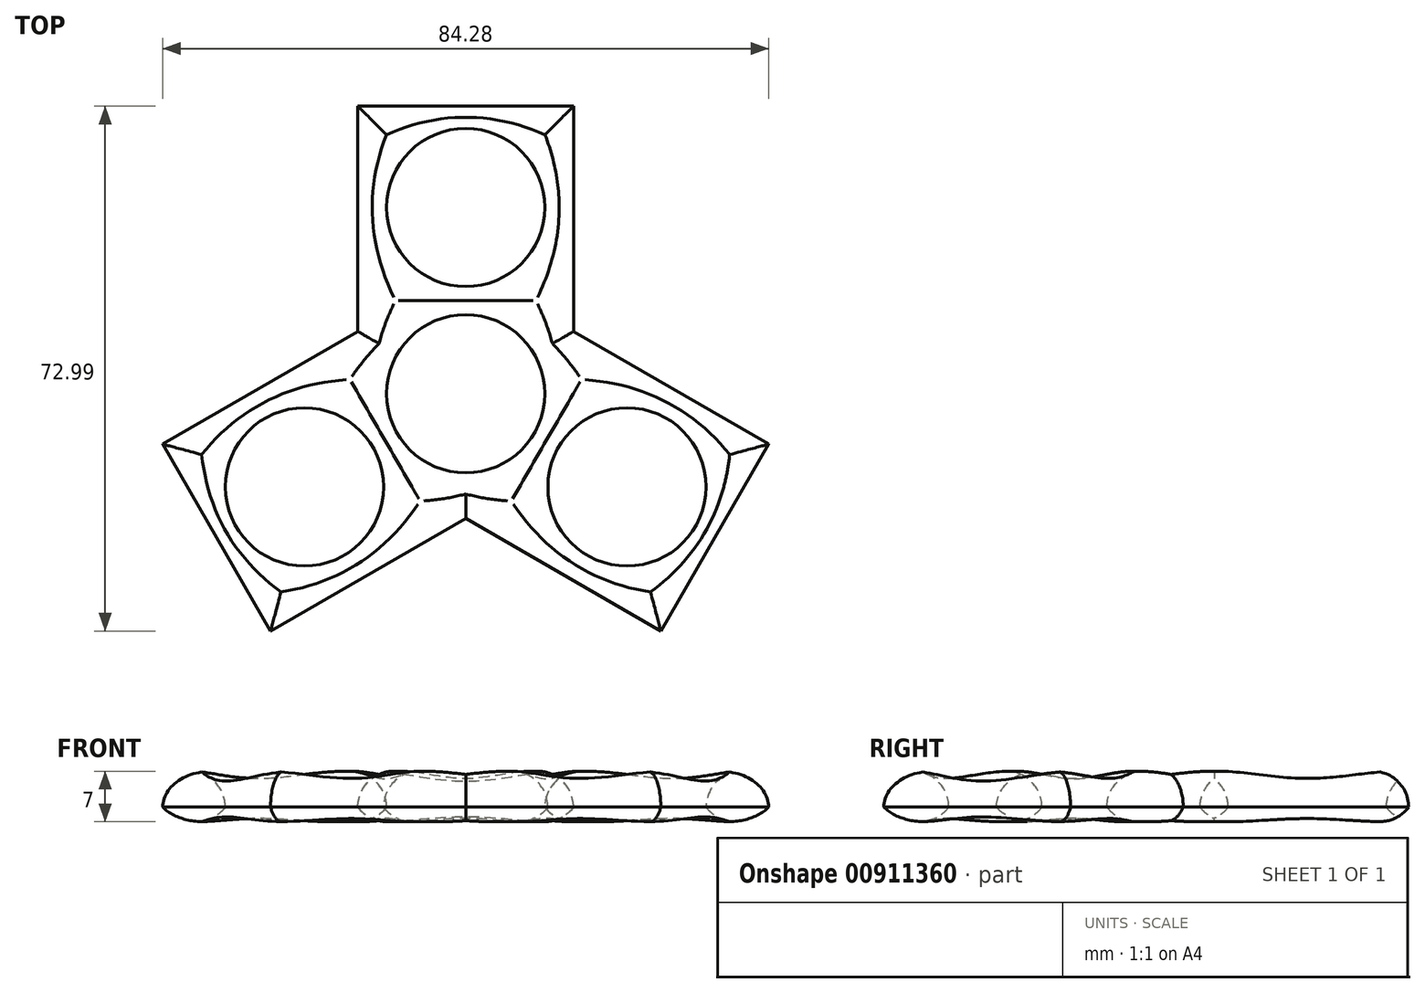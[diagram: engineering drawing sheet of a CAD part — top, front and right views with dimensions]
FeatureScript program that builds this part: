
annotation { "Feature Type Name" : "Feature", "Feature Type Description" : "" }
export const myFeature = defineFeature(function(context is Context, id is Id, definition is map)
    precondition{}
    {
        {
            var Q0;
            Q0=qCreatedBy(makeId("Top.planeOp"),FACE);
            var sketch = newSketch(context, id + "F0", { "sketchPlane" : qUnion([Q0])});
            skCircle(sketch, "E0", {"center": v(0, 0) * mm, "radius": 11 * mm});
            skLineSegment(sketch, "E1.bottom", {"start": v(0, 0) * mm, "end": v(15, 0) * mm});
            skLineSegment(sketch, "E1.top", {"start": v(0, 40) * mm, "end": v(15, 40) * mm});
            skLineSegment(sketch, "E1.left", {"start": v(0, 0) * mm, "end": v(0, 40) * mm});
            skLineSegment(sketch, "E1.right", {"start": v(15, 0) * mm, "end": v(15, 40) * mm});
            skLineSegment(sketch, "E2.bottom", {"start": v(0, 0) * mm, "end": v(-15, 0) * mm});
            skLineSegment(sketch, "E2.top", {"start": v(0, 40) * mm, "end": v(-15, 40) * mm});
            skLineSegment(sketch, "E2.right", {"start": v(-15, 0) * mm, "end": v(-15, 40) * mm});
            skLineSegment(sketch, "E3", {"start": v(0, 40) * mm, "end": v(0, 25.9) * mm});
            skCircle(sketch, "E4", {"center": v(0, 25.9) * mm, "radius": 11 * mm});
            skSolve(sketch);
        }
        {
            var Q0;
            {var subQ0=sQuery(id+"F0.wireOp",EDGE,"E2.top");Q0=makeQuery(id+"F0.imprint","IMPRINT",FACE,{"disambiguationData":[TD([[makeQuery(id+"F0.imprint","IMPRINT",EDGE,{"derivedFrom":subQ0}),1.0]])]});}
            var Q1;
            {var subQ9=sQuery(id+"F0.wireOp",EDGE,"E1.top");Q1=makeQuery(id+"F0.imprint","IMPRINT",FACE,{"disambiguationData":[TD([[makeQuery(id+"F0.imprint","IMPRINT",EDGE,{"derivedFrom":subQ9}),-1.0]])]});}
            extrude(context, id + "F1", {"entities" : qUnion([Q0, Q1]), "depth" : 7 * mm, "offsetDistance" : 25 * mm});
        }
        {
            var Q0;
            Q0=qCreatedBy(makeId("Front.planeOp"),FACE);
            var sketch = newSketch(context, id + "F2", { "sketchPlane" : qUnion([Q0])});
            skLineSegment(sketch, "E5", {"start": v(0, 30.21) * mm, "end": v(0, -19.5) * mm});
            skSolve(sketch);
        }
        {
            var Q0;
            Q0=makeQuery(id+"F1.opExtrude","SWEPT_BODY",BODY,{"disambiguationData":[OSD([sQuery(id+"F0.wireOp",EDGE,"E0"),sQuery(id+"F0.wireOp",EDGE,"E1.bottom"),sQuery(id+"F0.wireOp",EDGE,"E1.top"),sQuery(id+"F0.wireOp",EDGE,"E1.right"),sQuery(id+"F0.wireOp",EDGE,"E2.bottom"),sQuery(id+"F0.wireOp",EDGE,"E2.top"),sQuery(id+"F0.wireOp",EDGE,"E2.right"),sQuery(id+"F0.wireOp",EDGE,"E4")])]});
            var Q1;
            Q1=sQuery(id+"F2.wireOp",EDGE,"E5");
            var Q2;
            Q2=sQuery(id+"F2.wireOp",EDGE,"E5");
            transform(context, id + "F3", {"entities" : qUnion([Q0]), "transformType" : TransformType.ROTATION, "transformAxis" : qUnion([Q2]), "angle" : 120 * degree, "makeCopy" : true});
        }
        {
            var Q0;
            Q0=makeQuery(id+"F1.opExtrude","SWEPT_BODY",BODY,{"disambiguationData":[OSD([sQuery(id+"F0.wireOp",EDGE,"E0"),sQuery(id+"F0.wireOp",EDGE,"E1.bottom"),sQuery(id+"F0.wireOp",EDGE,"E1.top"),sQuery(id+"F0.wireOp",EDGE,"E1.right"),sQuery(id+"F0.wireOp",EDGE,"E2.bottom"),sQuery(id+"F0.wireOp",EDGE,"E2.top"),sQuery(id+"F0.wireOp",EDGE,"E2.right"),sQuery(id+"F0.wireOp",EDGE,"E4")])]});
            var Q1;
            Q1=sQuery(id+"F2.wireOp",EDGE,"E5");
            transform(context, id + "F4", {"entities" : qUnion([Q0]), "transformType" : TransformType.ROTATION, "transformAxis" : qUnion([Q1]), "angle" : 240 * degree, "makeCopy" : true});
        }
        {
            var Q0;
            Q0=makeQuery(id+"F1.opExtrude","SWEPT_BODY",BODY,{"disambiguationData":[OSD([sQuery(id+"F0.wireOp",EDGE,"E0"),sQuery(id+"F0.wireOp",EDGE,"E1.bottom"),sQuery(id+"F0.wireOp",EDGE,"E1.top"),sQuery(id+"F0.wireOp",EDGE,"E1.right"),sQuery(id+"F0.wireOp",EDGE,"E2.bottom"),sQuery(id+"F0.wireOp",EDGE,"E2.top"),sQuery(id+"F0.wireOp",EDGE,"E2.right"),sQuery(id+"F0.wireOp",EDGE,"E4")])]});
            var Q1;
            Q1=makeQuery(id+"F4.opPattern","COPY",BODY,{"derivedFrom":makeQuery(id+"F1.opExtrude","SWEPT_BODY",BODY,{"disambiguationData":[OSD([sQuery(id+"F0.wireOp",EDGE,"E0"),sQuery(id+"F0.wireOp",EDGE,"E1.bottom"),sQuery(id+"F0.wireOp",EDGE,"E1.top"),sQuery(id+"F0.wireOp",EDGE,"E1.right"),sQuery(id+"F0.wireOp",EDGE,"E2.bottom"),sQuery(id+"F0.wireOp",EDGE,"E2.top"),sQuery(id+"F0.wireOp",EDGE,"E2.right"),sQuery(id+"F0.wireOp",EDGE,"E4")])]}),"instanceName":"1"});
            var Q2;
            Q2=makeQuery(id+"F3.opPattern","COPY",BODY,{"derivedFrom":makeQuery(id+"F1.opExtrude","SWEPT_BODY",BODY,{"disambiguationData":[OSD([sQuery(id+"F0.wireOp",EDGE,"E0"),sQuery(id+"F0.wireOp",EDGE,"E1.bottom"),sQuery(id+"F0.wireOp",EDGE,"E1.top"),sQuery(id+"F0.wireOp",EDGE,"E1.right"),sQuery(id+"F0.wireOp",EDGE,"E2.bottom"),sQuery(id+"F0.wireOp",EDGE,"E2.top"),sQuery(id+"F0.wireOp",EDGE,"E2.right"),sQuery(id+"F0.wireOp",EDGE,"E4")])]}),"instanceName":"1"});
            booleanBodies(context, id + "F5", {"operationType" : BooleanOperationType.UNION, "tools" : qUnion([Q0, Q1, Q2])});
        }
        {
            var Q0;
            {var subQ0=makeQuery(id+"F1.opExtrude","CAP_FACE",FACE,{"disambiguationData":[OSD([sQuery(id+"F0.wireOp",EDGE,"E0"),sQuery(id+"F0.wireOp",EDGE,"E1.bottom"),sQuery(id+"F0.wireOp",EDGE,"E1.top"),sQuery(id+"F0.wireOp",EDGE,"E1.right"),sQuery(id+"F0.wireOp",EDGE,"E2.bottom"),sQuery(id+"F0.wireOp",EDGE,"E2.top"),sQuery(id+"F0.wireOp",EDGE,"E2.right"),sQuery(id+"F0.wireOp",EDGE,"E4")])],"isStart":false});Q0=makeQuery(id+"F5.opBoolean","MERGE",FACE,{"derivedFrom":[subQ0,makeQuery(id+"F3.opPattern","COPY",FACE,{"derivedFrom":subQ0,"instanceName":"1"}),makeQuery(id+"F4.opPattern","COPY",FACE,{"derivedFrom":subQ0,"instanceName":"1"})]});}
            fillet(context, id + "F6", {"entities" : qUnion([Q0]), "radius" : 5 * mm, "tangentPropagation" : true, "allowEdgeOverflow" : false});
        }
        {
            var Q0;
            {var subQ0=makeQuery(id+"F1.opExtrude","CAP_FACE",FACE,{"disambiguationData":[OSD([sQuery(id+"F0.wireOp",EDGE,"E0"),sQuery(id+"F0.wireOp",EDGE,"E1.bottom"),sQuery(id+"F0.wireOp",EDGE,"E1.top"),sQuery(id+"F0.wireOp",EDGE,"E1.right"),sQuery(id+"F0.wireOp",EDGE,"E2.bottom"),sQuery(id+"F0.wireOp",EDGE,"E2.top"),sQuery(id+"F0.wireOp",EDGE,"E2.right"),sQuery(id+"F0.wireOp",EDGE,"E4")])],"isStart":true});Q0=makeQuery(id+"F5.opBoolean","MERGE",FACE,{"derivedFrom":[subQ0,makeQuery(id+"F3.opPattern","COPY",FACE,{"derivedFrom":subQ0,"instanceName":"1"}),makeQuery(id+"F4.opPattern","COPY",FACE,{"derivedFrom":subQ0,"instanceName":"1"})]});}
            fillet(context, id + "F7", {"entities" : qUnion([Q0]), "radius" : 5 * mm, "tangentPropagation" : true, "allowEdgeOverflow" : false});
        }
    });
